# Revit family: Mast Light
name_source: partatom
category: Lighting Fixtures
revit_build: Autodesk Revit 2018 (Build: 20170223_1515(x64)
units: mm (PartAtom-declared; Revit-internal decimal feet)

## family parameters
Always vertical = Yes
Cut with Voids When Loaded = No
Host = Wall
Light Source = No
OmniClass Number = 23.80.70.00
OmniClass Title = Lighting
Part Type = Normal
Room Calculation Point = No
Round Connector Dimension = Use Diameter
Shared = No

## types (4) — shared parameters
ADA compliant = N / A
Dimmable = Mast Light
Lamp Dependant
Dimming Method = Lamp Dependant
Driver Required = No
Efficacy (lm/w) = Lamp Dependant
Electrical Class = 1
Lamp = GU10 LED
Light Source Fixed = No
Location / IP Rating = IP65
Main Material = Metal - Aluminium
Manufacturer = Astro Lighting Ltd
Manufacturer URL - Europe and Rest of World = www.astrolighting.com
Manufacturer URL - North America = us.astrolighting.com
Power (Watts) = 6 Watt MAX
Product CCT = Lamp Dependant
Product CRI = Lamp Dependant
Product Dimensions (MM) = 135 x 85 x 85
Product Location = Outdoor
Product Name = Mast Light
Product URL = https://www.astrolighting.com
Product Weight (KG) = 0.46
URL = www.astrolighting.com
Wattage Comments = -

## per-type parameters (varying)
| type | Main Finish | Product SKU |
| Mast Light Antique Brass | Antique Brass | 1317003 |
| Mast Light Textured Grey | Textured Grey | 1317007 |
| Mast Light Textured Black | Textured Black | 1317011 |
| Mast Light Textured White | Textured White | 1317012 |

## geometry (parser evidence)
native form markers: Sweep x2
no freeform markers — native parametric forms only
